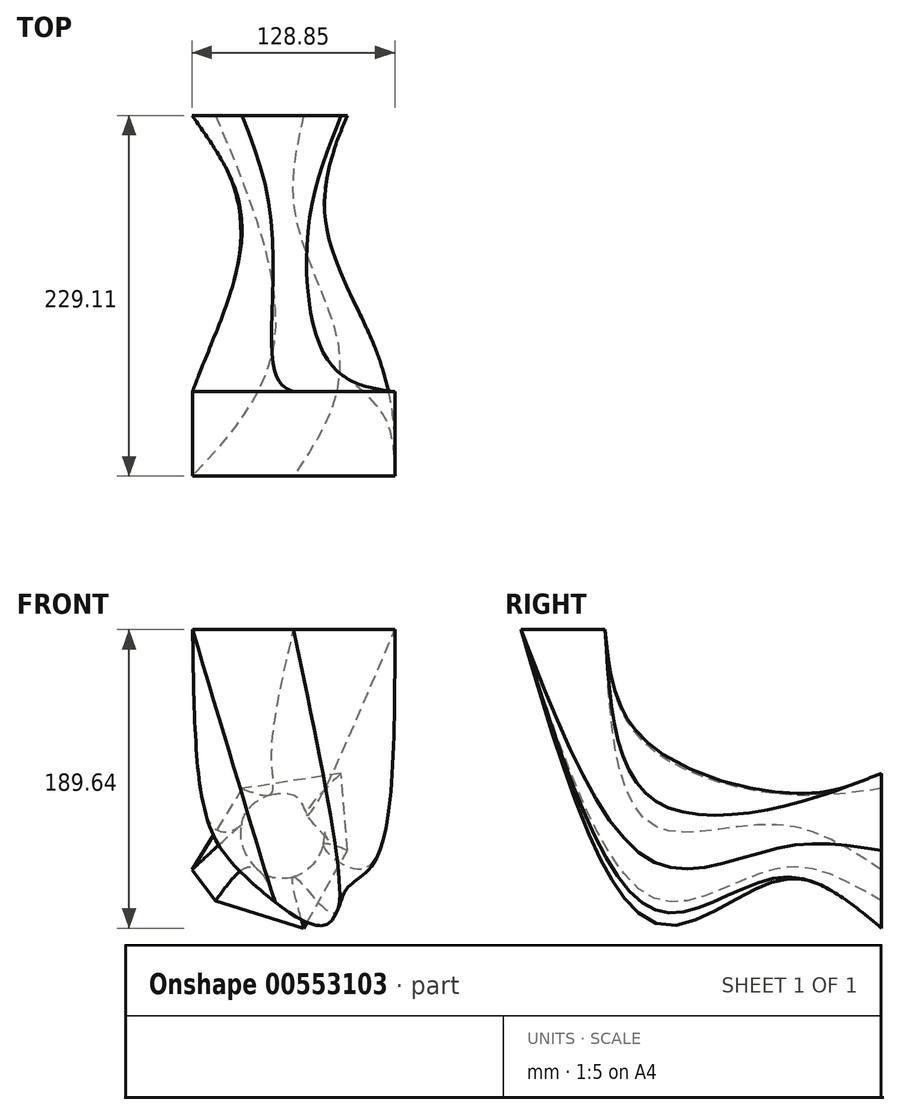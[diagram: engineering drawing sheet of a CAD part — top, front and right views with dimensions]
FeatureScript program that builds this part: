
annotation { "Feature Type Name" : "Feature", "Feature Type Description" : "" }
export const myFeature = defineFeature(function(context is Context, id is Id, definition is map)
    precondition{}
    {
        {
            var Q0;
            Q0=qCreatedBy(makeId("Front.planeOp"),FACE);
            var sketch = newSketch(context, id + "F0", { "sketchPlane" : qUnion([Q0])});
            skCircle(sketch, "E0", {"center": v(0, 0) * mm, "radius": 27.16 * mm});
            skSolve(sketch);
        }
        {
            var Q0;
            Q0=qCreatedBy(makeId("Front.planeOp"),FACE);
            cPlane(context, id + "F1", {"entities" : qUnion([Q0]), "cplaneType" : CPlaneType.OFFSET, "offset" : 58.67 * mm, "oppositeDirection" : true, "width" : 152.4 * mm, "height" : 152.4 * mm});
        }
        {
            var Q0;
            Q0=qCreatedBy(id+"F1.planeOp",FACE);
            var sketch = newSketch(context, id + "F2", { "sketchPlane" : qUnion([Q0])});
            skLineSegment(sketch, "E1", {"start": v(37.8, 39.75) * mm, "end": v(-25.13, 30.02) * mm});
            skLineSegment(sketch, "E2", {"start": v(-25.13, 30.02) * mm, "end": v(-57.02, -21.51) * mm});
            skLineSegment(sketch, "E3", {"start": v(-57.02, -21.51) * mm, "end": v(-42.04, -41.38) * mm});
            skLineSegment(sketch, "E4", {"start": v(-42.04, -41.38) * mm, "end": v(14.02, -58.58) * mm});
            skLineSegment(sketch, "E5", {"start": v(14.02, -58.58) * mm, "end": v(41.75, -9.2) * mm});
            skLineSegment(sketch, "E6", {"start": v(41.75, -9.2) * mm, "end": v(37.8, 39.75) * mm});
            skSolve(sketch);
        }
        {
            var Q0;
            Q0=qCreatedBy(makeId("Front.planeOp"),FACE);
            cPlane(context, id + "F3", {"entities" : qUnion([Q0]), "cplaneType" : CPlaneType.OFFSET, "offset" : 84.07 * mm, "width" : 152.4 * mm, "height" : 152.4 * mm});
        }
        {
            var Q0;
            Q0=qCreatedBy(id+"F3.planeOp",FACE);
            var sketch = newSketch(context, id + "F4", { "sketchPlane" : qUnion([Q0])});
            skFitSpline(sketch, "E7", {"points": [v(27.22, 14.1) * mm, v(57.27, -17.68) * mm, v(41.74, -32.84) * mm, v(29.52, -55.13) * mm, v(-21.94, -26.15) * mm, v(-42.04, 16.53) * mm, v(4.63, 54.3) * mm, v(27.22, 14.1) * mm]});
            skSolve(sketch);
        }
        {
            var Q0;
            Q0=qCreatedBy(makeId("Top.planeOp"),FACE);
            cPlane(context, id + "F5", {"entities" : qUnion([Q0]), "cplaneType" : CPlaneType.OFFSET, "offset" : 131.06 * mm, "width" : 152.4 * mm, "height" : 152.4 * mm});
        }
        {
            var Q0;
            Q0=qCreatedBy(id+"F5.planeOp",FACE);
            var sketch = newSketch(context, id + "F6", { "sketchPlane" : qUnion([Q0])});
            skLineSegment(sketch, "E8.bottom", {"start": v(71.83, -170.44) * mm, "end": v(-56.62, -170.44) * mm});
            skLineSegment(sketch, "E8.top", {"start": v(71.83, -116.87) * mm, "end": v(-56.62, -116.87) * mm});
            skLineSegment(sketch, "E8.left", {"start": v(71.83, -170.44) * mm, "end": v(71.83, -116.87) * mm});
            skLineSegment(sketch, "E8.right", {"start": v(-56.62, -170.44) * mm, "end": v(-56.62, -116.87) * mm});
            skSolve(sketch);
        }
        {
            var Q0;
            Q0=makeQuery(id+"F2.imprint","IMPRINT",FACE,{"disambiguationData":[TD([[makeQuery(id+"F2.imprint","IMPRINT",EDGE,{"derivedFrom":sQuery(id+"F2.wireOp",EDGE,"E1")}),1.0]])]});
            var Q1;
            Q1=makeQuery(id+"F0.imprint","IMPRINT",FACE,{"disambiguationData":[TD([[makeQuery(id+"F0.imprint","IMPRINT",EDGE,{"derivedFrom":sQuery(id+"F0.wireOp",EDGE,"E0")}),1.0]])]});
            var Q2;
            Q2=makeQuery(id+"F4.imprint","IMPRINT",FACE,{"disambiguationData":[TD([[makeQuery(id+"F4.imprint","IMPRINT",EDGE,{"derivedFrom":sQuery(id+"F4.wireOp",EDGE,"E7")}),-1.0]])]});
            var Q3;
            Q3=makeQuery(id+"F6.imprint","IMPRINT",FACE,{"disambiguationData":[TD([[makeQuery(id+"F6.imprint","IMPRINT",EDGE,{"derivedFrom":sQuery(id+"F6.wireOp",EDGE,"E8.bottom")}),-1.0]])]});
            loft(context, id + "F7", {"sheetProfilesArray" : [{ "sheetProfileEntities" : qUnion([Q0]) }, { "sheetProfileEntities" : qUnion([Q1]) }, { "sheetProfileEntities" : qUnion([Q2]) }, { "sheetProfileEntities" : qUnion([Q3]) }]});
        }
    });
